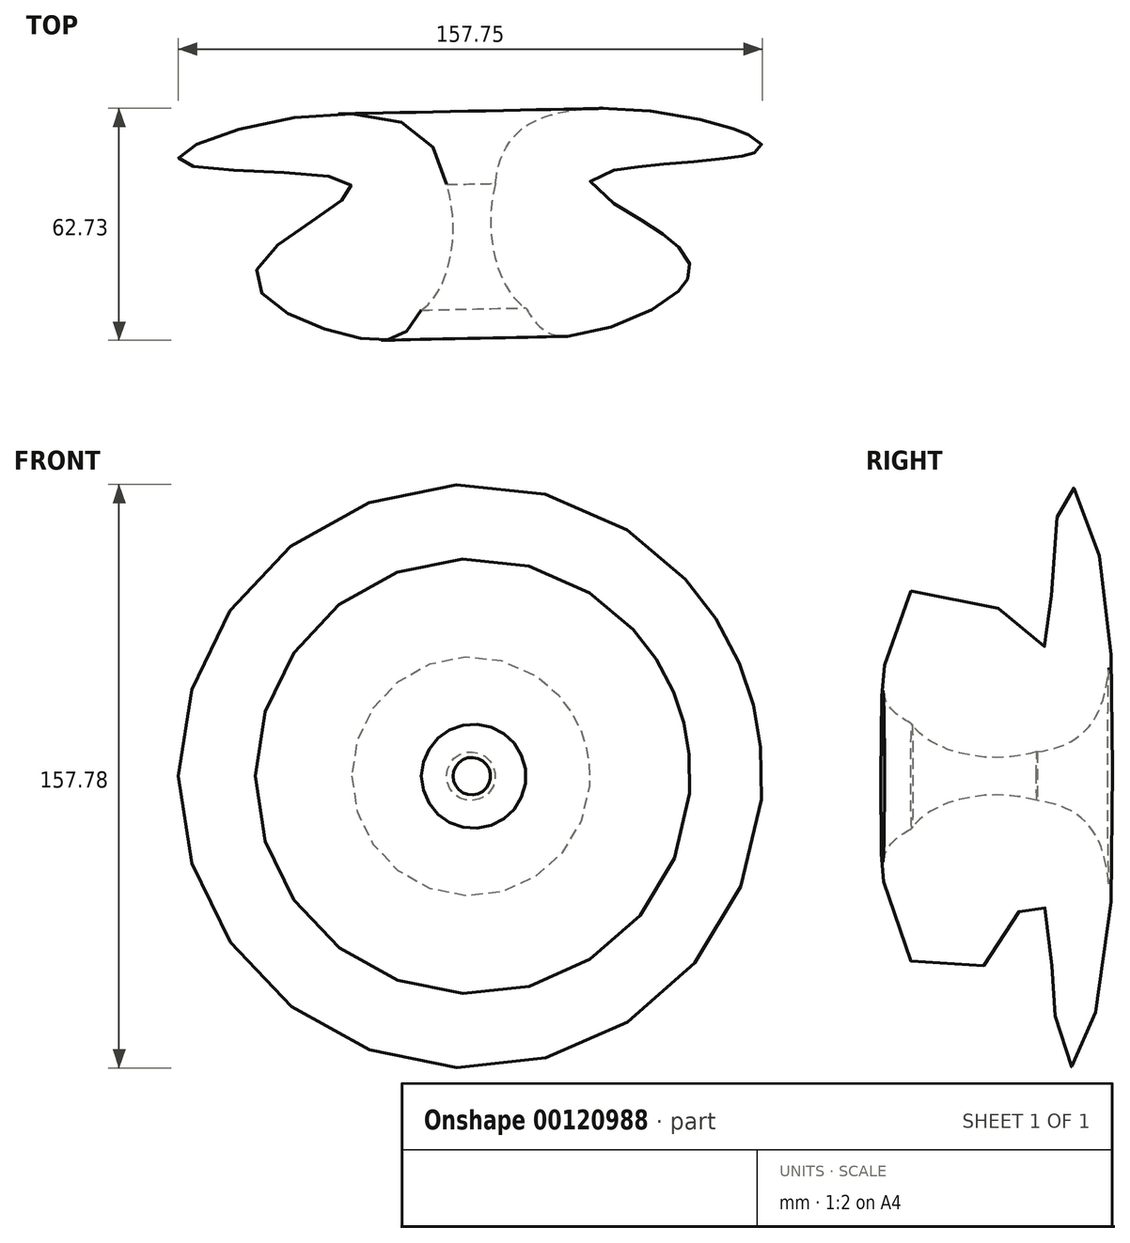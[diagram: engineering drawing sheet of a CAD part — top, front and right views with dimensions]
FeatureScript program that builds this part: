
annotation { "Feature Type Name" : "Feature", "Feature Type Description" : "" }
export const myFeature = defineFeature(function(context is Context, id is Id, definition is map)
    precondition{}
    {
        {
            var Q0;
            Q0=qCreatedBy(makeId("Top.planeOp"),FACE);
            var sketch = newSketch(context, id + "F0", { "sketchPlane" : qUnion([Q0])});
            skEllipse(sketch, "E0", {"center": v(-17.68, 15.55) * mm, "majorRadius": 23.67 * mm, "minorRadius": 13.3 * mm, "majorAxis": v(0, -1)});
            skFitSpline(sketch, "E1", {"points": [v(-15.69, 42.93) * mm, v(-78.44, 33.8) * mm, v(-31.95, 27.24) * mm, v(-57.62, 3.85) * mm, v(-28.24, -14.4) * mm, v(-12.96, -6.58) * mm, v(-15.69, 42.93) * mm]});
            skSolve(sketch);
        }
        {
            var Q0;
            Q0=qCreatedBy(makeId("Top.planeOp"),FACE);
            var sketch = newSketch(context, id + "F1", { "sketchPlane" : qUnion([Q0])});
            skLineSegment(sketch, "E2", {"start": v(0, 48.63) * mm, "end": v(2, -46.35) * mm});
            skLineSegment(sketch, "E3", {"start": v(2, -46.35) * mm, "end": v(-2.57, -49.77) * mm});
            skSolve(sketch);
        }
        {
            var Q0;
            {var subQ0=sQuery(id+"F0.wireOp",EDGE,"E1");var subQ1=sQuery(id+"F0.wireOp",EDGE,"E0");var subQ2=makeQuery(id+"F0.imprint","INTERSECT",VERTEX,{"disambiguationData":[OD(0.0)],"derivedFrom":[subQ1,subQ0]});Q0=makeQuery(id+"F0.imprint","IMPRINT",FACE,{"disambiguationData":[TD([[makeQuery(id+"F0.imprint","IMPRINT",EDGE,{"disambiguationData":[TD([[subQ2,-1.0]])],"derivedFrom":subQ1}),1.0]])]});}
            var Q1;
            {var subQ0=sQuery(id+"F0.wireOp",EDGE,"E1");var subQ1=sQuery(id+"F0.wireOp",EDGE,"E0");var subQ2=makeQuery(id+"F0.imprint","INTERSECT",VERTEX,{"disambiguationData":[OD(0.0)],"derivedFrom":[subQ1,subQ0]});Q1=makeQuery(id+"F0.imprint","IMPRINT",FACE,{"disambiguationData":[TD([[makeQuery(id+"F0.imprint","IMPRINT",EDGE,{"disambiguationData":[TD([[subQ2,1.0]])],"derivedFrom":subQ1}),1.0]])]});}
            var Q2;
            {var subQ0=sQuery(id+"F0.wireOp",EDGE,"E1");var subQ1=sQuery(id+"F0.wireOp",EDGE,"E0");var subQ2=makeQuery(id+"F0.imprint","INTERSECT",VERTEX,{"disambiguationData":[OD(0.0)],"derivedFrom":[subQ1,subQ0]});Q2=makeQuery(id+"F0.imprint","IMPRINT",FACE,{"disambiguationData":[TD([[makeQuery(id+"F0.imprint","IMPRINT",EDGE,{"disambiguationData":[TD([[subQ2,1.0]])],"derivedFrom":subQ1}),-1.0]])]});}
            var Q3;
            Q3=sQuery(id+"F1.wireOp",EDGE,"E2");
            revolve(context, id + "F2", {"entities" : qUnion([Q0, Q1, Q2]), "axis" : qUnion([Q3]), "revolveType" : RevolveType.FULL});
        }
    });
